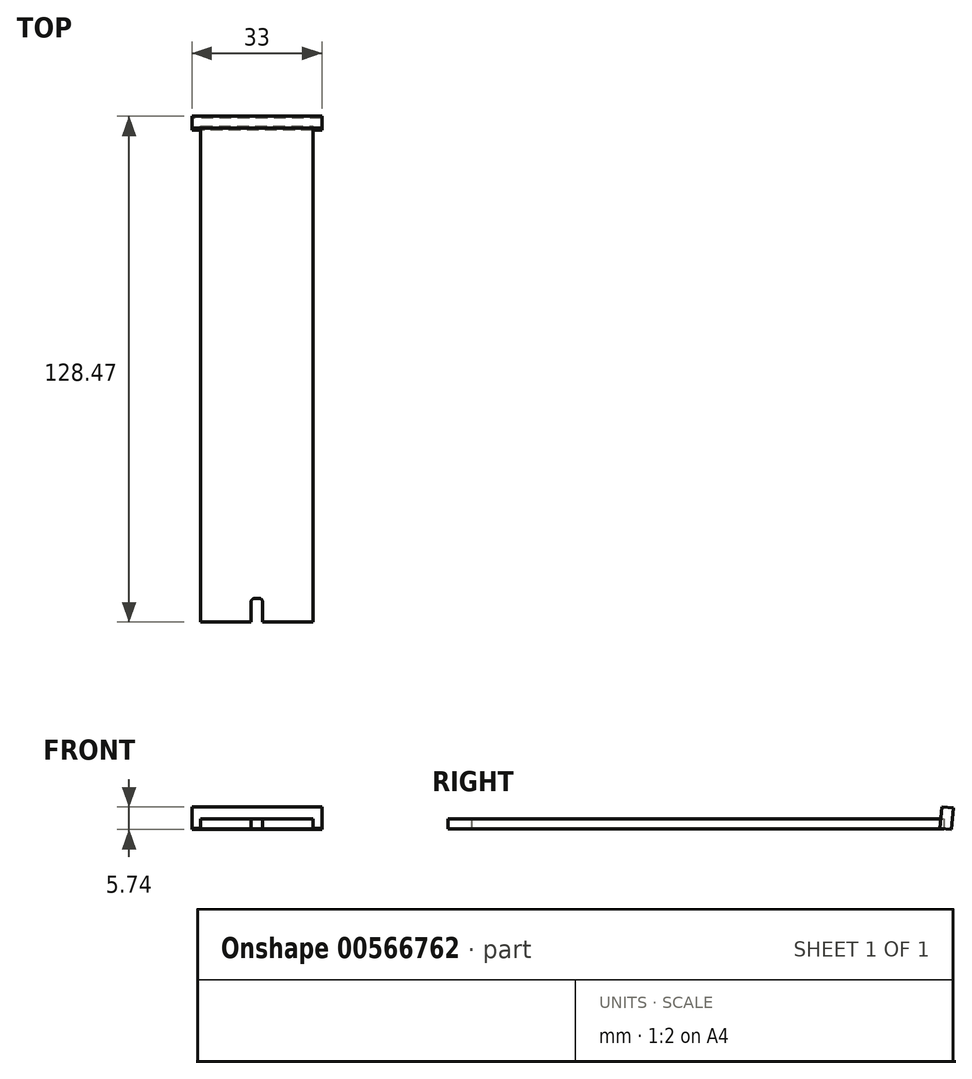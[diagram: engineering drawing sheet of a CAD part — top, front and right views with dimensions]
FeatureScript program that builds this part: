
annotation { "Feature Type Name" : "Feature", "Feature Type Description" : "" }
export const myFeature = defineFeature(function(context is Context, id is Id, definition is map)
    precondition{}
    {
        {
            var Q0;
            Q0=qCreatedBy(makeId("Top.planeOp"),FACE);
            var sketch = newSketch(context, id + "F0", { "sketchPlane" : qUnion([Q0])});
            skLineSegment(sketch, "E0.bottom", {"start": v(-23.7, -57.67) * mm, "end": v(-10.94, -57.67) * mm});
            skLineSegment(sketch, "E0.top", {"start": v(-23.7, 68.33) * mm, "end": v(4.8, 68.33) * mm});
            skLineSegment(sketch, "E0.left", {"start": v(-23.7, -57.67) * mm, "end": v(-23.7, 68.33) * mm});
            skLineSegment(sketch, "E0.right", {"start": v(4.8, -57.67) * mm, "end": v(4.8, 68.33) * mm});
            skPoint(sketch, "E1.oppositeSnap0", {"position": v(-10.94, -57.67) * mm});
            skLineSegment(sketch, "E1.top", {"start": v(-7.94, -51.67) * mm, "end": v(-10.94, -51.67) * mm});
            skLineSegment(sketch, "E1.left", {"start": v(-7.94, -57.67) * mm, "end": v(-7.94, -51.67) * mm});
            skLineSegment(sketch, "E1.right", {"start": v(-10.94, -57.67) * mm, "end": v(-10.94, -51.67) * mm});
            skLineSegment(sketch, "E2.trimOffspring", {"start": v(-7.94, -57.67) * mm, "end": v(4.8, -57.67) * mm});
            skPoint(sketch, "E3", {"position": v(-9.44, 68.33) * mm});
            skSolve(sketch);
        }
        {
            var Q0;
            Q0 = qSketchRegion(id + "F0", true);
            extrude(context, id + "F1", {"entities" : qUnion([Q0]), "depth" : 2.5 * mm, "offsetDistance" : 25 * mm});
        }
        {
            var Q0;
            Q0=makeQuery(id+"F1.opExtrude","SWEPT_EDGE",EDGE,{"disambiguationData":[OSD([sQuery(id+"F0.wireOp",EDGE,"E1.top"),sQuery(id+"F0.wireOp",EDGE,"E1.right")])]});
            var Q1;
            Q1=makeQuery(id+"F1.opExtrude","SWEPT_EDGE",EDGE,{"disambiguationData":[OSD([sQuery(id+"F0.wireOp",EDGE,"E1.top"),sQuery(id+"F0.wireOp",EDGE,"E1.left")])]});
            fillet(context, id + "F2", {"entities" : qUnion([Q0, Q1]), "radius" : 1 * mm, "tangentPropagation" : true, "allowEdgeOverflow" : false});
        }
        {
            var Q0;
            Q0=makeQuery(id+"F1.opExtrude","CAP_EDGE",EDGE,{"disambiguationData":[OSD([sQuery(id+"F0.wireOp",EDGE,"E0.top")])],"isStart":true});
            cPlane(context, id + "F3", {"entities" : qUnion([Q0]), "cplaneType" : CPlaneType.LINE_ANGLE, "offset" : 25 * mm, "angle" : 175 * degree, "width" : 150 * mm, "height" : 150 * mm});
        }
        {
            var Q0;
            Q0=qCreatedBy(id+"F3.planeOp",FACE);
            var sketch = newSketch(context, id + "F4", { "sketchPlane" : qUnion([Q0])});
            skLineSegment(sketch, "E4.bottom", {"start": v(7.06, 11.46) * mm, "end": v(-25.94, 11.46) * mm});
            skLineSegment(sketch, "E4.top", {"start": v(7.06, 5.96) * mm, "end": v(-25.94, 5.96) * mm});
            skLineSegment(sketch, "E4.left", {"start": v(7.06, 11.46) * mm, "end": v(7.06, 5.96) * mm});
            skLineSegment(sketch, "E4.right", {"start": v(-25.94, 11.46) * mm, "end": v(-25.94, 5.96) * mm});
            skPoint(sketch, "E5", {"position": v(-9.44, 5.96) * mm});
            skSolve(sketch);
        }
        {
            var Q0;
            Q0 = qSketchRegion(id + "F4", true);
            extrude(context, id + "F5", {"entities" : qUnion([Q0]), "oppositeDirection" : true, "depth" : 2 * mm, "offsetDistance" : 25 * mm, "hasSecondDirection" : true, "secondDirectionOppositeDirection" : false, "secondDirectionDepth" : 1 * mm});
        }
    });
